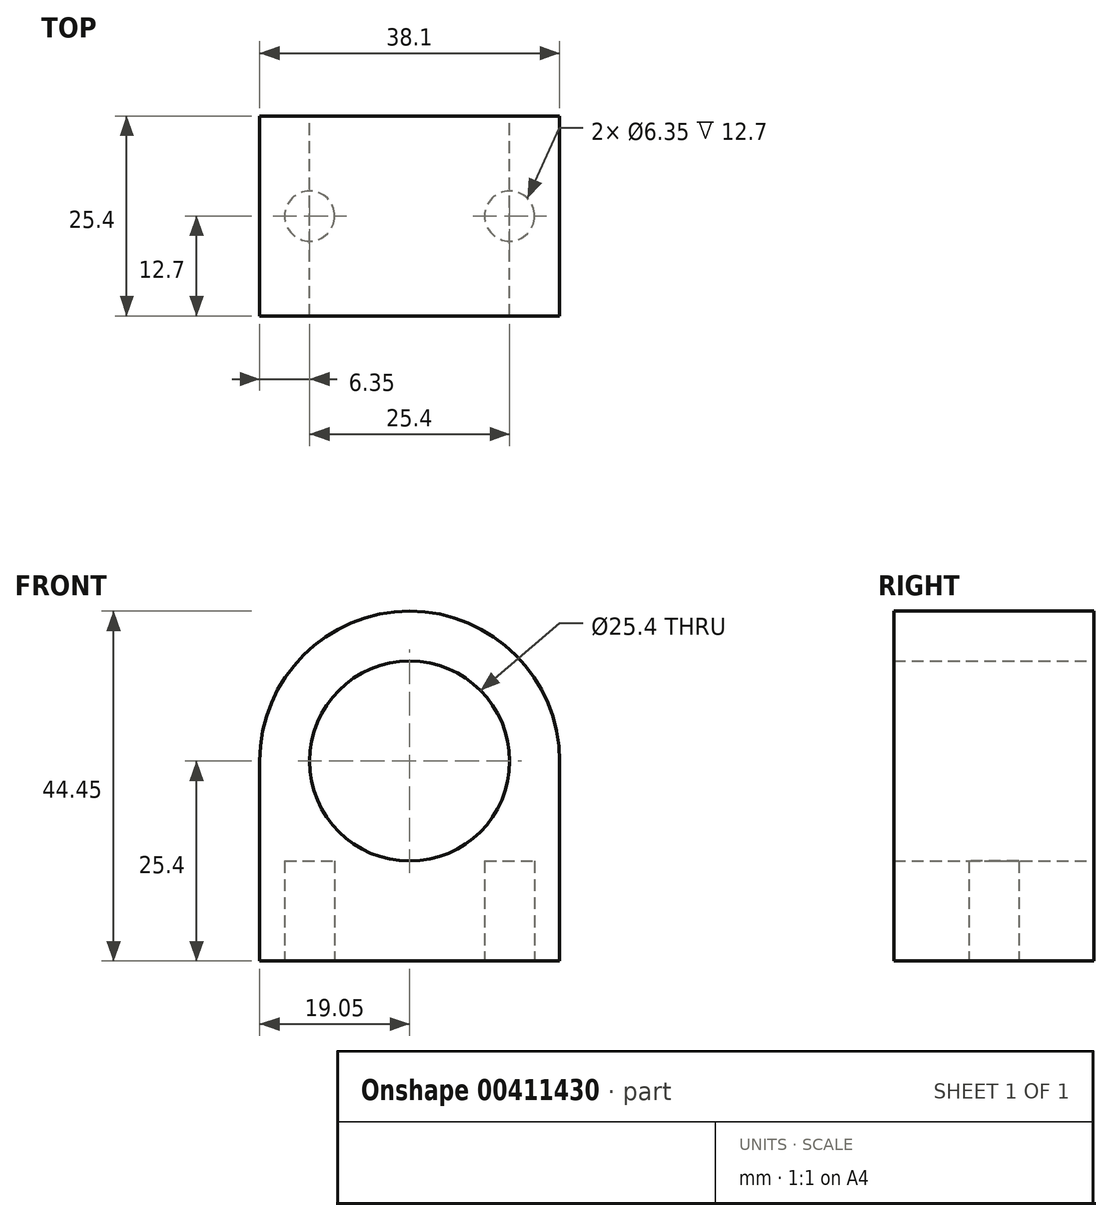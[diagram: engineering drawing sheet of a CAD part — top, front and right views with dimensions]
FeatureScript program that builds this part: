
annotation { "Feature Type Name" : "Feature", "Feature Type Description" : "" }
export const myFeature = defineFeature(function(context is Context, id is Id, definition is map)
    precondition{}
    {
        {
            var Q0;
            Q0=qCreatedBy(makeId("Front.planeOp"),FACE);
            var sketch = newSketch(context, id + "F0", { "sketchPlane" : qUnion([Q0])});
            skArc(sketch, "E0", {"start": v(19.05, 0) * mm, "mid": v(0, 19.05) * mm, "end": v(-19.05, 0) * mm});
            skLineSegment(sketch, "E1.top", {"start": v(-19.05, -25.4) * mm, "end": v(19.05, -25.4) * mm});
            skLineSegment(sketch, "E1.left", {"start": v(-19.05, 0) * mm, "end": v(-19.05, -25.4) * mm});
            skLineSegment(sketch, "E1.right", {"start": v(19.05, 0) * mm, "end": v(19.05, -25.4) * mm});
            skCircle(sketch, "E2", {"center": v(0, 0) * mm, "radius": 12.7 * mm});
            skSolve(sketch);
        }
        {
            var Q0;
            Q0=makeQuery(id+"F0.imprint","IMPRINT",FACE,{"disambiguationData":[TD([[makeQuery(id+"F0.imprint","IMPRINT",EDGE,{"derivedFrom":sQuery(id+"F0.wireOp",EDGE,"E0")}),1.0]])]});
            extrude(context, id + "F1", {"entities" : qUnion([Q0]), "depth" : 25.4 * mm});
        }
        {
            var Q0;
            Q0=makeQuery(id+"F1.opExtrude","SWEPT_FACE",FACE,{"disambiguationData":[OSD([sQuery(id+"F0.wireOp",EDGE,"E1.top")])]});
            var sketch = newSketch(context, id + "F2", { "sketchPlane" : qUnion([Q0])});
            skCircle(sketch, "E3", {"center": v(-12.7, 12.7) * mm, "radius": 3.18 * mm});
            skCircle(sketch, "E4", {"center": v(12.7, 12.7) * mm, "radius": 3.18 * mm});
            skSolve(sketch);
        }
        {
            var Q0;
            Q0 = qSketchRegion(id + "F2", true);
            extrude(context, id + "F3", {"entities" : qUnion([Q0]), "operationType" : NewBodyOperationType.REMOVE, "oppositeDirection" : true, "depth" : 12.7 * mm});
        }
    });
